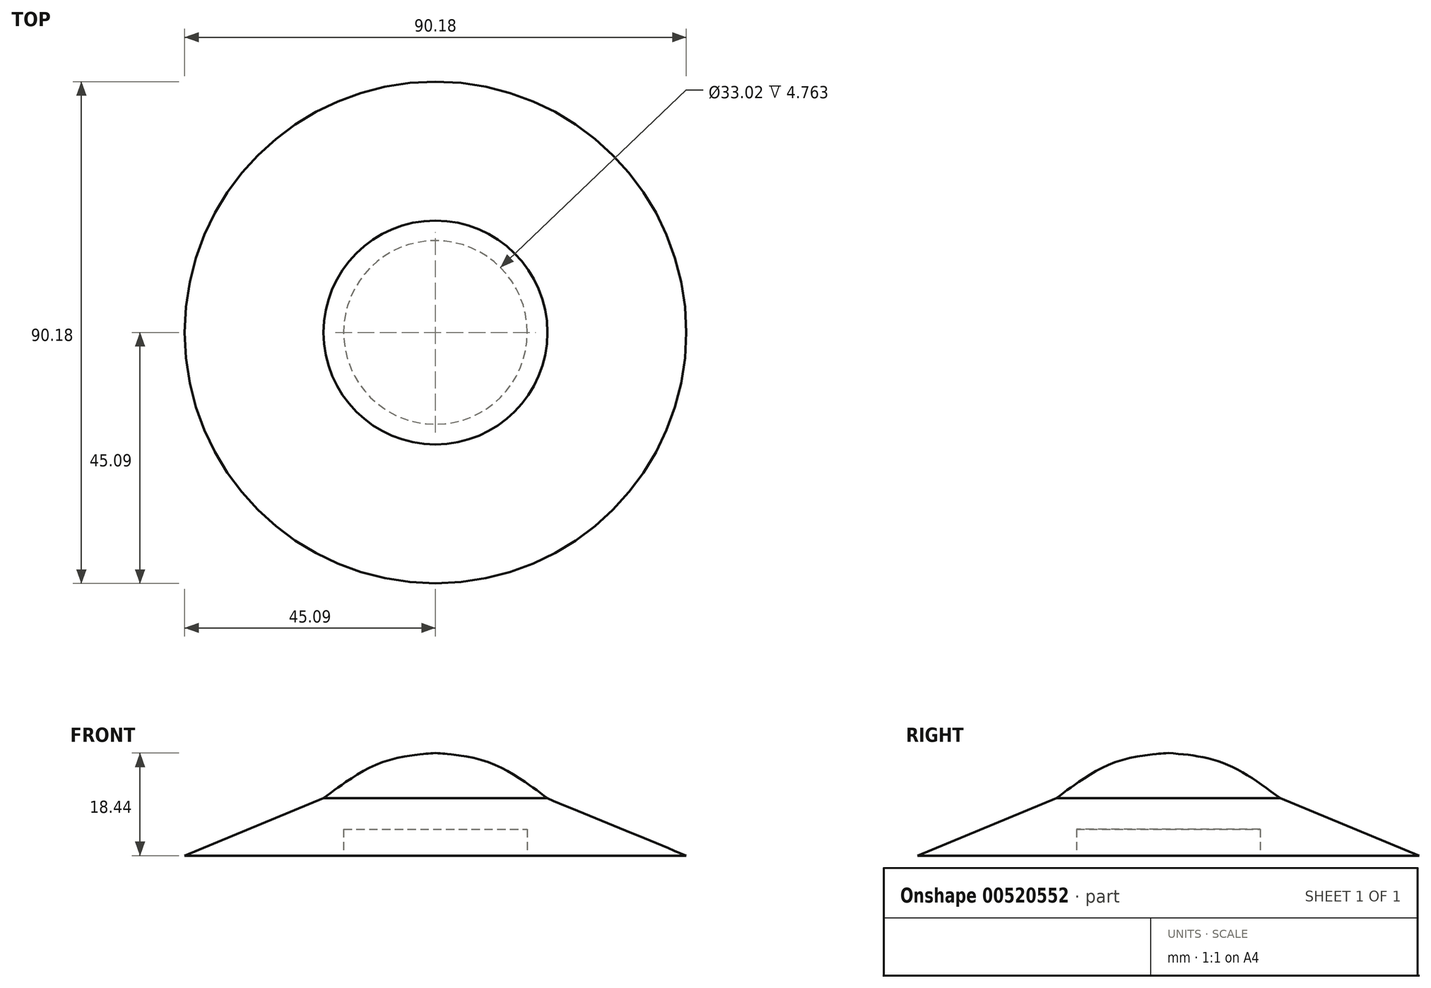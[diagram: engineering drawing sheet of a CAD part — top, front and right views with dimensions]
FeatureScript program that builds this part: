
annotation { "Feature Type Name" : "Feature", "Feature Type Description" : "" }
export const myFeature = defineFeature(function(context is Context, id is Id, definition is map)
    precondition{}
    {
        {
            var Q0;
            Q0=qCreatedBy(makeId("Right.planeOp"),FACE);
            var sketch = newSketch(context, id + "F0", { "sketchPlane" : qUnion([Q0])});
            skLineSegment(sketch, "E0", {"start": v(19.68, 0) * mm, "end": v(0, 0) * mm});
            skFitSpline(sketch, "E1", {"points": [v(20.13, 10.3) * mm, v(9.74, 16.7) * mm, v(0, 18.44) * mm], "startDerivative": vector(-18.87, 14.48) * mm, "endDerivative": vector(-20.72, 1.6) * mm});
            skLineSegment(sketch, "E2", {"start": v(0, 18.44) * mm, "end": v(0, 0) * mm});
            skLineSegment(sketch, "E3", {"start": v(19.68, 0) * mm, "end": v(45.09, 0) * mm});
            skLineSegment(sketch, "E4", {"start": v(45.09, 0) * mm, "end": v(20.13, 10.3) * mm});
            skSolve(sketch);
        }
        {
            var Q0;
            Q0=makeQuery(id+"F0.imprint","IMPRINT",FACE,{"disambiguationData":[TD([[makeQuery(id+"F0.imprint","IMPRINT",EDGE,{"derivedFrom":sQuery(id+"F0.wireOp",EDGE,"E0")}),-1.0]])]});
            var Q1;
            Q1=sQuery(id+"F0.wireOp",EDGE,"E2");
            revolve(context, id + "F1", {"entities" : qUnion([Q0]), "axis" : qUnion([Q1]), "revolveType" : RevolveType.FULL});
        }
        {
            var Q0;
            Q0=makeQuery(id+"F1.opRevolve","SWEPT_FACE",FACE,{"disambiguationData":[OSD([sQuery(id+"F0.wireOp",EDGE,"E0"),sQuery(id+"F0.wireOp",EDGE,"E3")])]});
            var sketch = newSketch(context, id + "F2", { "sketchPlane" : qUnion([Q0])});
            skCircle(sketch, "E5", {"center": v(0, 0) * mm, "radius": 16.51 * mm});
            skSolve(sketch);
        }
        {
            var Q0;
            Q0 = qSketchRegion(id + "F2", true);
            extrude(context, id + "F3", {"entities" : qUnion([Q0]), "operationType" : NewBodyOperationType.REMOVE, "oppositeDirection" : true, "depth" : 4.76 * mm, "offsetDistance" : 25.4 * mm});
        }
    });
